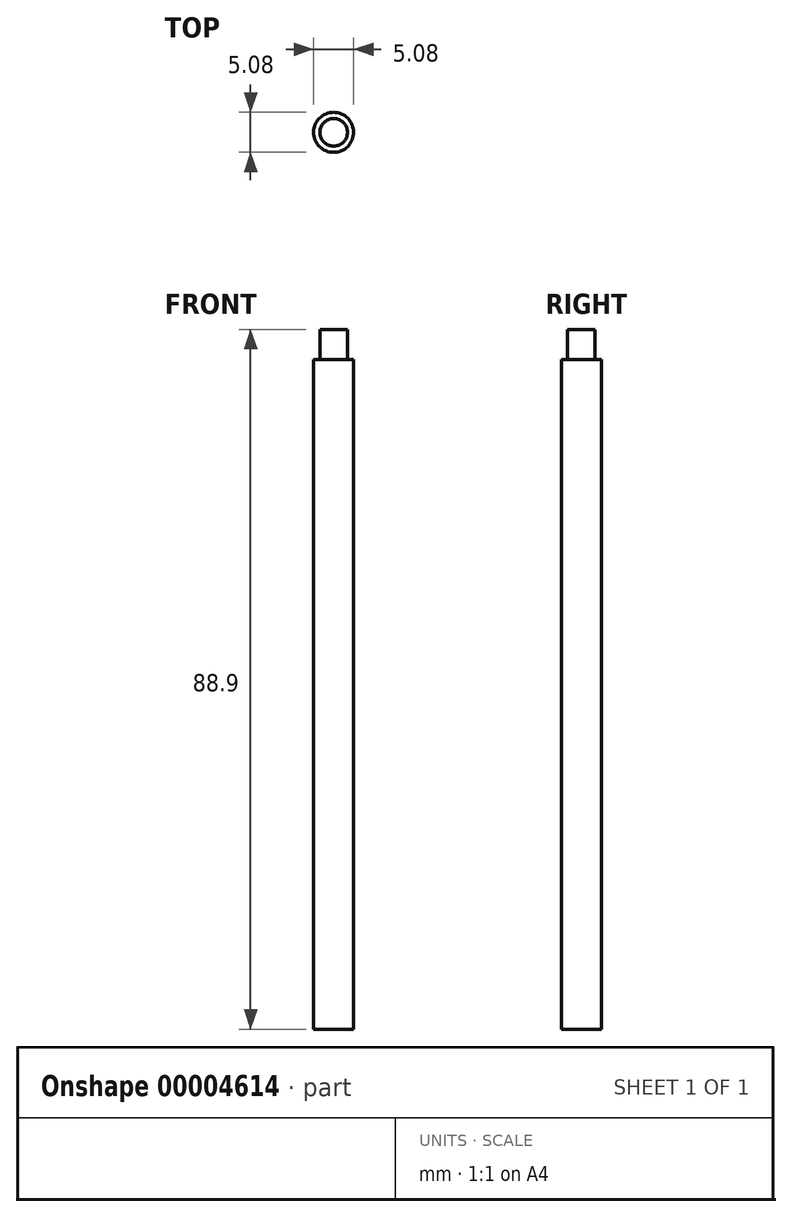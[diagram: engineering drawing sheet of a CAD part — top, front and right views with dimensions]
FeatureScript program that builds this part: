
annotation { "Feature Type Name" : "Feature", "Feature Type Description" : "" }
export const myFeature = defineFeature(function(context is Context, id is Id, definition is map)
    precondition{}
    {
        {
            var Q0;
            Q0=qCreatedBy(makeId("Front.planeOp"),FACE);
            var sketch = newSketch(context, id + "F0", { "sketchPlane" : qUnion([Q0])});
            skLineSegment(sketch, "E0", {"start": v(0, 0) * mm, "end": v(0, 88.9) * mm});
            skLineSegment(sketch, "E1", {"start": v(0, 88.9) * mm, "end": v(1.75, 88.9) * mm});
            skLineSegment(sketch, "E2", {"start": v(1.75, 88.9) * mm, "end": v(1.75, 85.1) * mm});
            skLineSegment(sketch, "E3", {"start": v(1.75, 85.1) * mm, "end": v(2.54, 85.1) * mm});
            skLineSegment(sketch, "E4", {"start": v(2.54, 85.1) * mm, "end": v(2.54, 0) * mm});
            skLineSegment(sketch, "E5", {"start": v(2.54, 0) * mm, "end": v(0, 0) * mm});
            skSolve(sketch);
        }
        {
            var Q0;
            Q0 = qSketchRegion(id + "F0", true);
            var Q1;
            Q1=sQuery(id+"F0.wireOp",EDGE,"E0");
            revolve(context, id + "F1", {"entities" : qUnion([Q0]), "axis" : qUnion([Q1]), "revolveType" : RevolveType.FULL});
        }
    });
